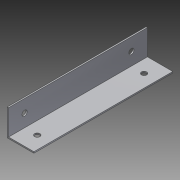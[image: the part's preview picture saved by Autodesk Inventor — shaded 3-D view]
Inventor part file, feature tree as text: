
AUTODESK INVENTOR PART (.ipt)
format: ipt  version: 2014 SP1 (Build 180222100, 222)  size: 101,888 bytes
history: native  units: in
note: dims shown in document units (in); Inventor stores cm internally (conversion verified against a paired STEP export)
features: extrude x3, sketch x3
ambient origin geometry x8: Origin, YZ Plane, XZ Plane, XY Plane, X Axis, Y Axis, Z Axis, Center Point
bodies: Solid1 (feature_tree)
feature tree (6):
  extrude  "Extrusion1"  Depth=0.0312in
  sketch  "Sketch2"  dims[d2=3.25in d3=0.0in d4=0.375in]
  sketch  "Sketch3"  dims[d5=0.125in d6=3.25in d7=0.7874in d9=2.5in d10=0.3937in d12=1.0in d14=0.125in d15=0.375in d16=3.25in d17=0.7874in d19=2.5in d20=0.3937in d22=1.0in d24=1.0in d25=0.0in d26=1.0in d27=0.0in]
  extrude  "Extrusion2"  Depth=3.25in
  extrude  "Extrusion3"  Depth=3.25in
  sketch  "Sketch1"  dims[d0=0.625in d1=0.0312in]
